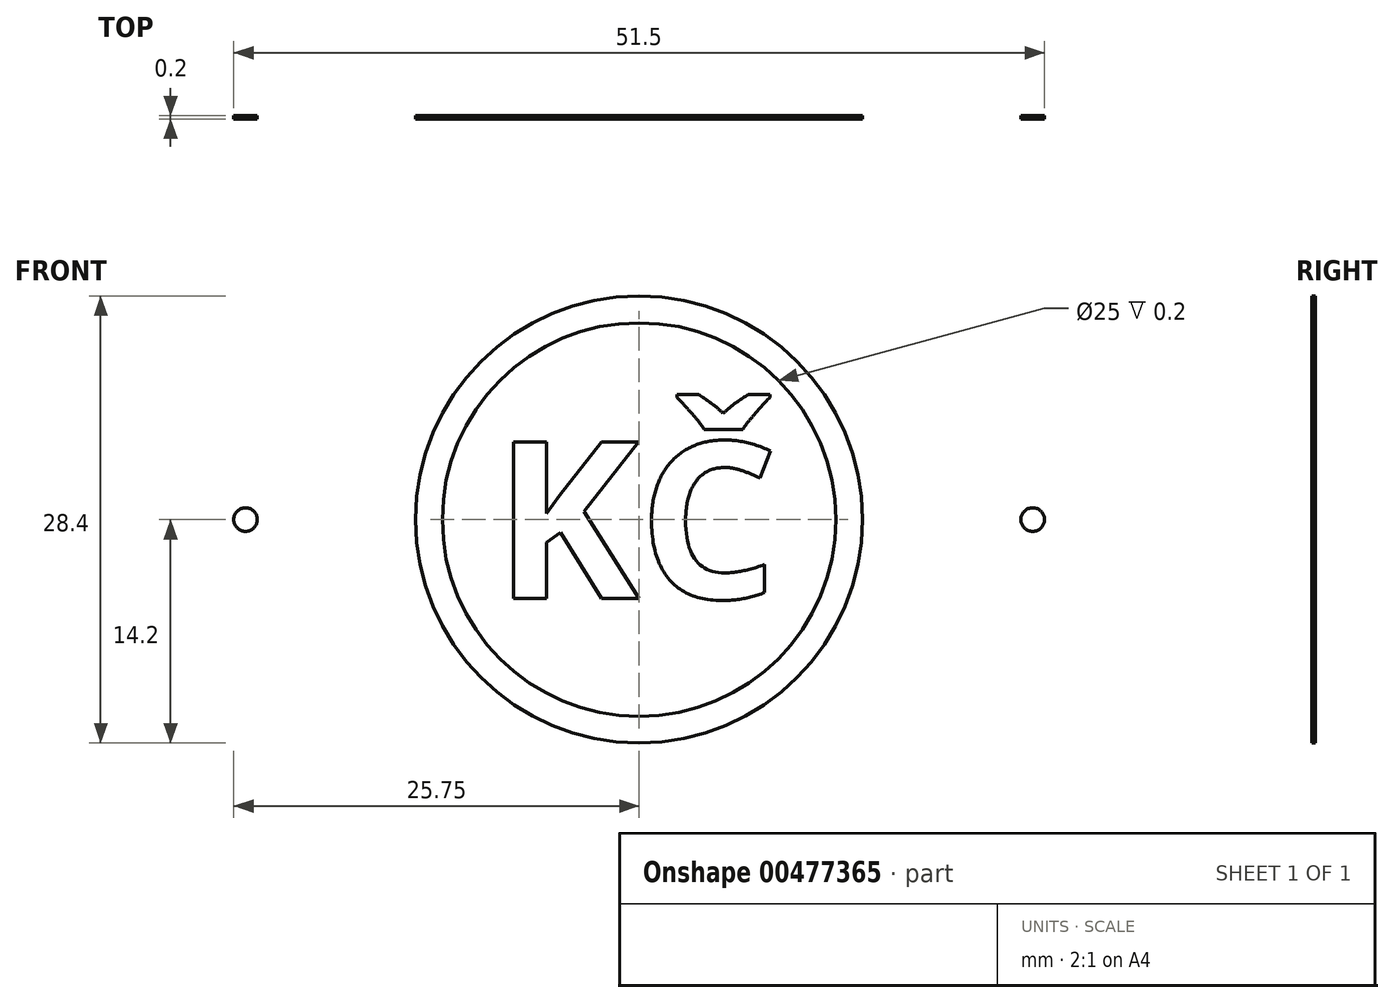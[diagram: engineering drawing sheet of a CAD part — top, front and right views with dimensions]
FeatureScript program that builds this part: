
annotation { "Feature Type Name" : "Feature", "Feature Type Description" : "" }
export const myFeature = defineFeature(function(context is Context, id is Id, definition is map)
    precondition{}
    {
        {
            var Q0;
            Q0=qCreatedBy(makeId("Front.planeOp"),FACE);
            var sketch = newSketch(context, id + "F0", { "sketchPlane" : qUnion([Q0])});
            skCircle(sketch, "E0", {"center": v(-25, 0) * mm, "radius": 0.75 * mm});
            skCircle(sketch, "E1", {"center": v(0, 0) * mm, "radius": 12.5 * mm});
            skCircle(sketch, "E2", {"center": v(0, 0) * mm, "radius": 14.2 * mm});
            skCircle(sketch, "E3", {"center": v(25, 0) * mm, "radius": 0.75 * mm});
            skText(sketch, "E4", { "text": "KČ", "fontName": "OpenSans-Bold.ttf"});
            const initialGuessF0  = {"E4": [-0.00924, -0.005, 1, 0, 0.01]};
            skSetInitialGuess(sketch, initialGuessF0);
            skSolve(sketch);
        }
        {
            var Q0;
            Q0 = qSketchRegion(id + "F0", true);
            var Q1;
            Q1=makeQuery(id+"F0.imprint","IMPRINT",FACE,{"disambiguationData":[TD([[makeQuery(id+"F0.imprint","IMPRINT",EDGE,{"derivedFrom":sQuery(id+"F0.wireOp",EDGE,"E4.sketch_text.stroke-0")}),-1.0]])]});
            var Q2;
            Q2=makeQuery(id+"F0.imprint","IMPRINT",FACE,{"disambiguationData":[TD([[makeQuery(id+"F0.imprint","IMPRINT",EDGE,{"derivedFrom":sQuery(id+"F0.wireOp",EDGE,"E4.sketch_text.stroke-13")}),-1.0]])]});
            var Q3;
            Q3=makeQuery(id+"F0.imprint","IMPRINT",FACE,{"disambiguationData":[TD([[makeQuery(id+"F0.imprint","IMPRINT",EDGE,{"derivedFrom":sQuery(id+"F0.wireOp",EDGE,"E4.sketch_text.stroke-28")}),-1.0]])]});
            extrude(context, id + "F1", {"entities" : qUnion([Q0, Q1, Q2, Q3]), "oppositeDirection" : true, "depth" : 0.2 * mm});
        }
    });
